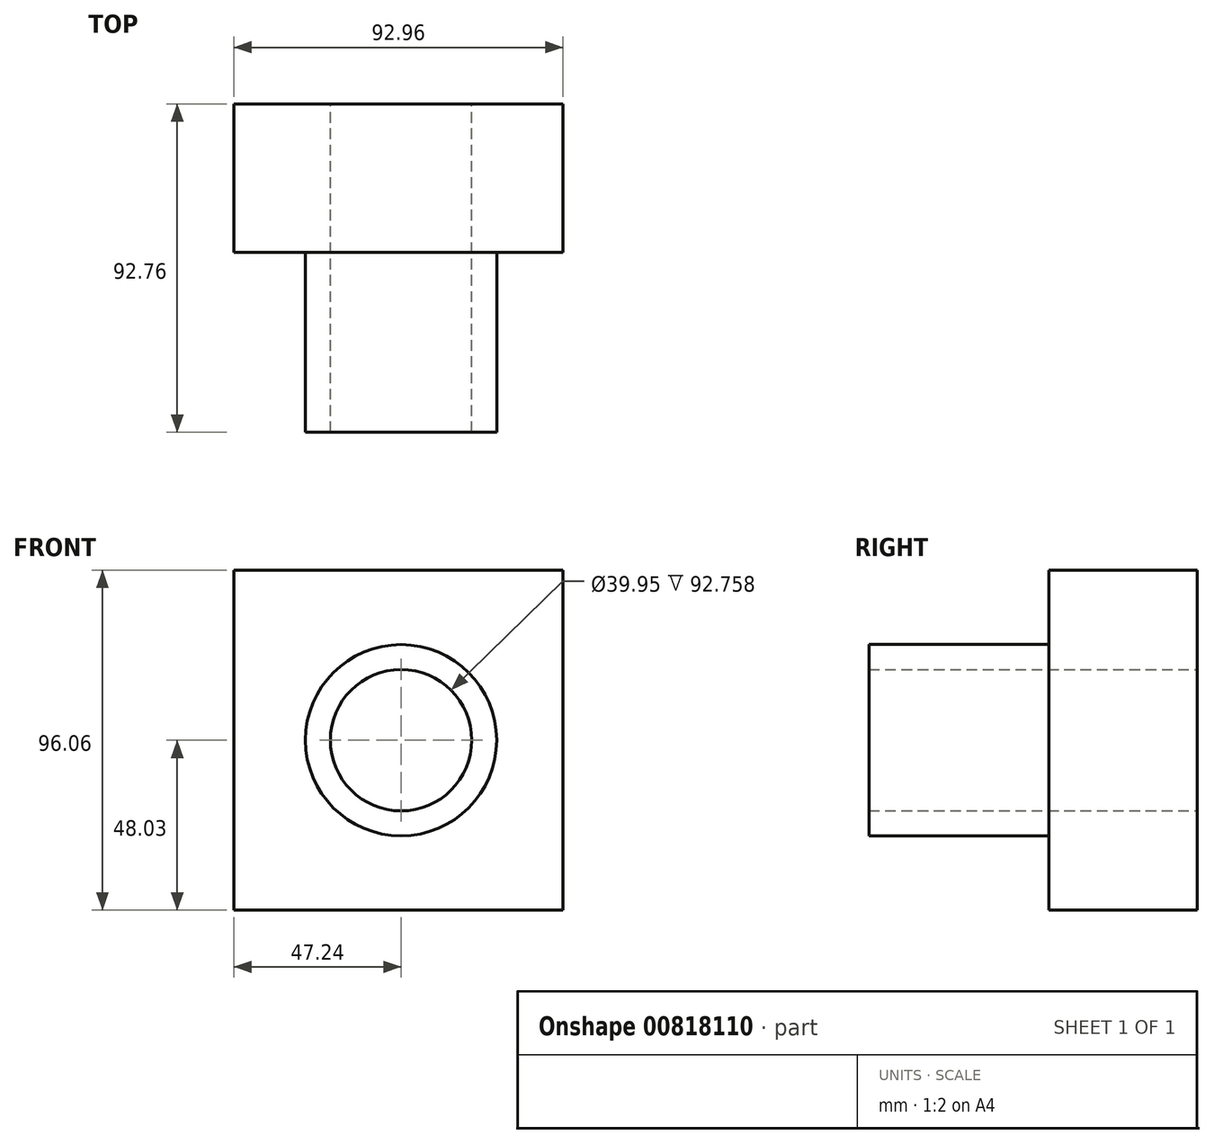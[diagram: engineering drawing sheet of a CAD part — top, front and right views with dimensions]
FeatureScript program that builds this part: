
annotation { "Feature Type Name" : "Feature", "Feature Type Description" : "" }
export const myFeature = defineFeature(function(context is Context, id is Id, definition is map)
    precondition{}
    {
        {
            var Q0;
            Q0=qCreatedBy(makeId("Right.planeOp"),FACE);
            var sketch = newSketch(context, id + "F0", { "sketchPlane" : qUnion([Q0])});
            skLineSegment(sketch, "E0.bottom", {"start": v(20.98, 48.03) * mm, "end": v(-20.98, 48.03) * mm});
            skLineSegment(sketch, "E0.top", {"start": v(20.98, -48.03) * mm, "end": v(-20.98, -48.03) * mm});
            skLineSegment(sketch, "E0.left", {"start": v(20.98, 48.03) * mm, "end": v(20.98, -48.03) * mm});
            skLineSegment(sketch, "E0.right", {"start": v(-20.98, 48.03) * mm, "end": v(-20.98, -48.03) * mm});
            skPoint(sketch, "E0.middle", {"position": v(0, 0) * mm});
            skSolve(sketch);
        }
        {
            var Q0;
            Q0=qSketchRegion(id+"F0",true);
            extrude(context, id + "F1", {"entities" : qUnion([Q0]), "depth" : 45.72 * mm, "offsetDistance" : 25.4 * mm});
        }
        {
            var Q0;
            Q0=makeQuery(id+"F1.opExtrude","CAP_FACE",FACE,{"disambiguationData":[OSD([sQuery(id+"F0.wireOp",EDGE,"E0.bottom"),sQuery(id+"F0.wireOp",EDGE,"E0.top"),sQuery(id+"F0.wireOp",EDGE,"E0.left"),sQuery(id+"F0.wireOp",EDGE,"E0.right")])],"isStart":true});
            extrude(context, id + "F2", {"entities" : qUnion([Q0]), "operationType" : NewBodyOperationType.ADD, "depth" : 47.24 * mm, "offsetDistance" : 25.4 * mm});
        }
        {
            var Q0;
            {var subQ0=sQuery(id+"F0.wireOp",EDGE,"E0.right");Q0=makeQuery(id+"F2.boolean.opBoolean","MERGE",FACE,{"derivedFrom":[makeQuery(id+"F1.opExtrude","SWEPT_FACE",FACE,{"disambiguationData":[OSD([subQ0])]}),makeQuery(id+"F2.opExtrude","SWEPT_FACE",FACE,{"disambiguationData":[OSD([subQ0])]})]});}
            var sketch = newSketch(context, id + "F3", { "sketchPlane" : qUnion([Q0])});
            skCircle(sketch, "E1", {"center": v(0, 0) * mm, "radius": 27.01 * mm});
            skCircle(sketch, "E2", {"center": v(0, 0) * mm, "radius": 19.97 * mm});
            skSolve(sketch);
        }
        {
            var Q0;
            Q0=makeQuery(id+"F3.imprint","IMPRINT",FACE,{"disambiguationData":[TD([[makeQuery(id+"F3.imprint","IMPRINT",EDGE,{"derivedFrom":sQuery(id+"F3.wireOp",EDGE,"E1")}),1.0]])]});
            extrude(context, id + "F4", {"entities" : qUnion([Q0]), "operationType" : NewBodyOperationType.ADD, "depth" : 50.8 * mm, "offsetDistance" : 25.4 * mm});
        }
        {
            var Q0;
            {var subQ0=sQuery(id+"F0.wireOp",EDGE,"E0.right");Q0=makeQuery(id+"F4.boolean.opBoolean","SPLIT",FACE,{"disambiguationData":[TD([makeQuery(id+"F4.opExtrude","SWEPT_FACE",FACE,{"disambiguationData":[OSD([sQuery(id+"F3.wireOp",EDGE,"E2")])]})])],"derivedFrom":makeQuery(id+"F2.boolean.opBoolean","MERGE",FACE,{"derivedFrom":[makeQuery(id+"F1.opExtrude","SWEPT_FACE",FACE,{"disambiguationData":[OSD([subQ0])]}),makeQuery(id+"F2.opExtrude","SWEPT_FACE",FACE,{"disambiguationData":[OSD([subQ0])]})]})});}
            extrude(context, id + "F5", {"entities" : qUnion([Q0]), "operationType" : NewBodyOperationType.REMOVE, "oppositeDirection" : true, "depth" : 76.7 * mm, "offsetDistance" : 25.4 * mm});
        }
    });
